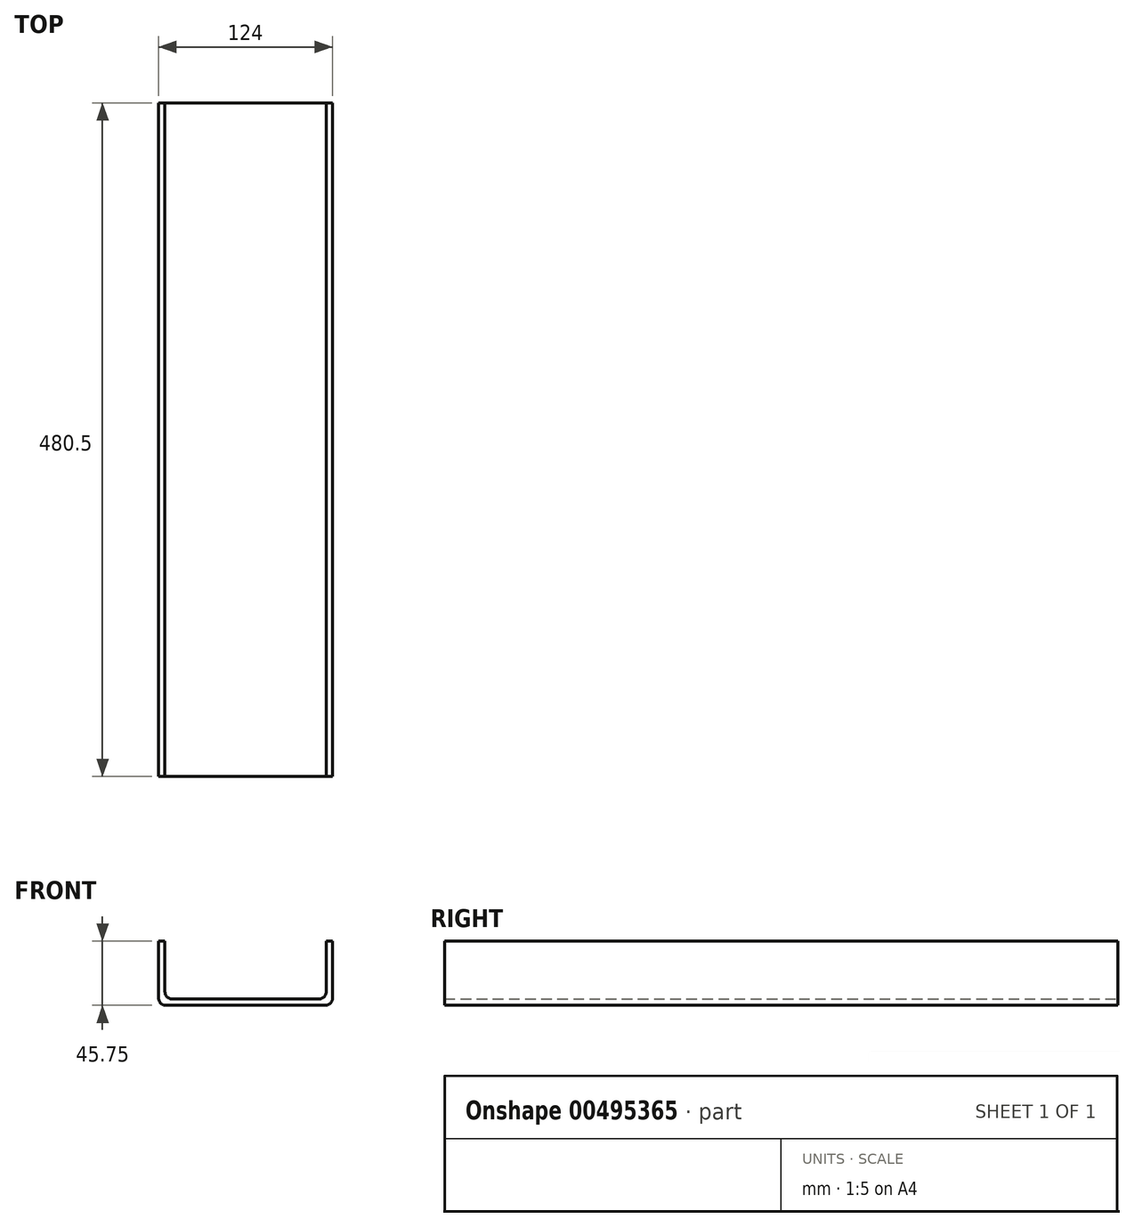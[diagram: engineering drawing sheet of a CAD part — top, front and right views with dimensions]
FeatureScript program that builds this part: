
annotation { "Feature Type Name" : "Feature", "Feature Type Description" : "" }
export const myFeature = defineFeature(function(context is Context, id is Id, definition is map)
    precondition{}
    {
        {
            var Q0;
            Q0=qCreatedBy(makeId("Front.planeOp"),FACE);
            var sketch = newSketch(context, id + "F0", { "sketchPlane" : qUnion([Q0])});
            skLineSegment(sketch, "E0", {"start": v(5, 0) * mm, "end": v(119, 0) * mm});
            skLineSegment(sketch, "E1", {"start": v(0, 5) * mm, "end": v(0, 45.75) * mm});
            skLineSegment(sketch, "E2", {"start": v(124, 5) * mm, "end": v(124, 45.75) * mm});
            skLineSegment(sketch, "E3.0", {"start": v(4.5, 9.5) * mm, "end": v(4.5, 45.75) * mm});
            skLineSegment(sketch, "E3.1", {"start": v(9.5, 4.5) * mm, "end": v(114.5, 4.5) * mm});
            skLineSegment(sketch, "E3.2", {"start": v(119.5, 9.5) * mm, "end": v(119.5, 45.75) * mm});
            skPoint(sketch, "E4.visualSharp", {"position": v(0, 0) * mm});
            skArc(sketch, "E4.filletArc", {"start": v(0, 5) * mm, "mid": v(1.46, 1.46) * mm, "end": v(5, 0) * mm});
            skPoint(sketch, "E5.visualSharp", {"position": v(4.5, 4.5) * mm});
            skArc(sketch, "E5.filletArc", {"start": v(4.5, 9.5) * mm, "mid": v(5.96, 5.96) * mm, "end": v(9.5, 4.5) * mm});
            skPoint(sketch, "E6.visualSharp", {"position": v(119.5, 4.5) * mm});
            skArc(sketch, "E6.filletArc", {"start": v(114.5, 4.5) * mm, "mid": v(118.04, 5.96) * mm, "end": v(119.5, 9.5) * mm});
            skPoint(sketch, "E7.visualSharp", {"position": v(124, 0) * mm});
            skArc(sketch, "E7.filletArc", {"start": v(119, 0) * mm, "mid": v(122.54, 1.46) * mm, "end": v(124, 5) * mm});
            skLineSegment(sketch, "E8", {"start": v(0, 45.75) * mm, "end": v(4.5, 45.75) * mm});
            skLineSegment(sketch, "E9", {"start": v(119.5, 45.75) * mm, "end": v(124, 45.75) * mm});
            skSolve(sketch);
        }
        {
            var Q0;
            Q0=makeQuery(id+"F0.imprint","IMPRINT",FACE,{"disambiguationData":[TD([[makeQuery(id+"F0.imprint","IMPRINT",EDGE,{"derivedFrom":sQuery(id+"F0.wireOp",EDGE,"E0")}),1.0]])]});
            extrude(context, id + "F1", {"entities" : qUnion([Q0]), "depth" : 480.5 * mm});
        }
    });
